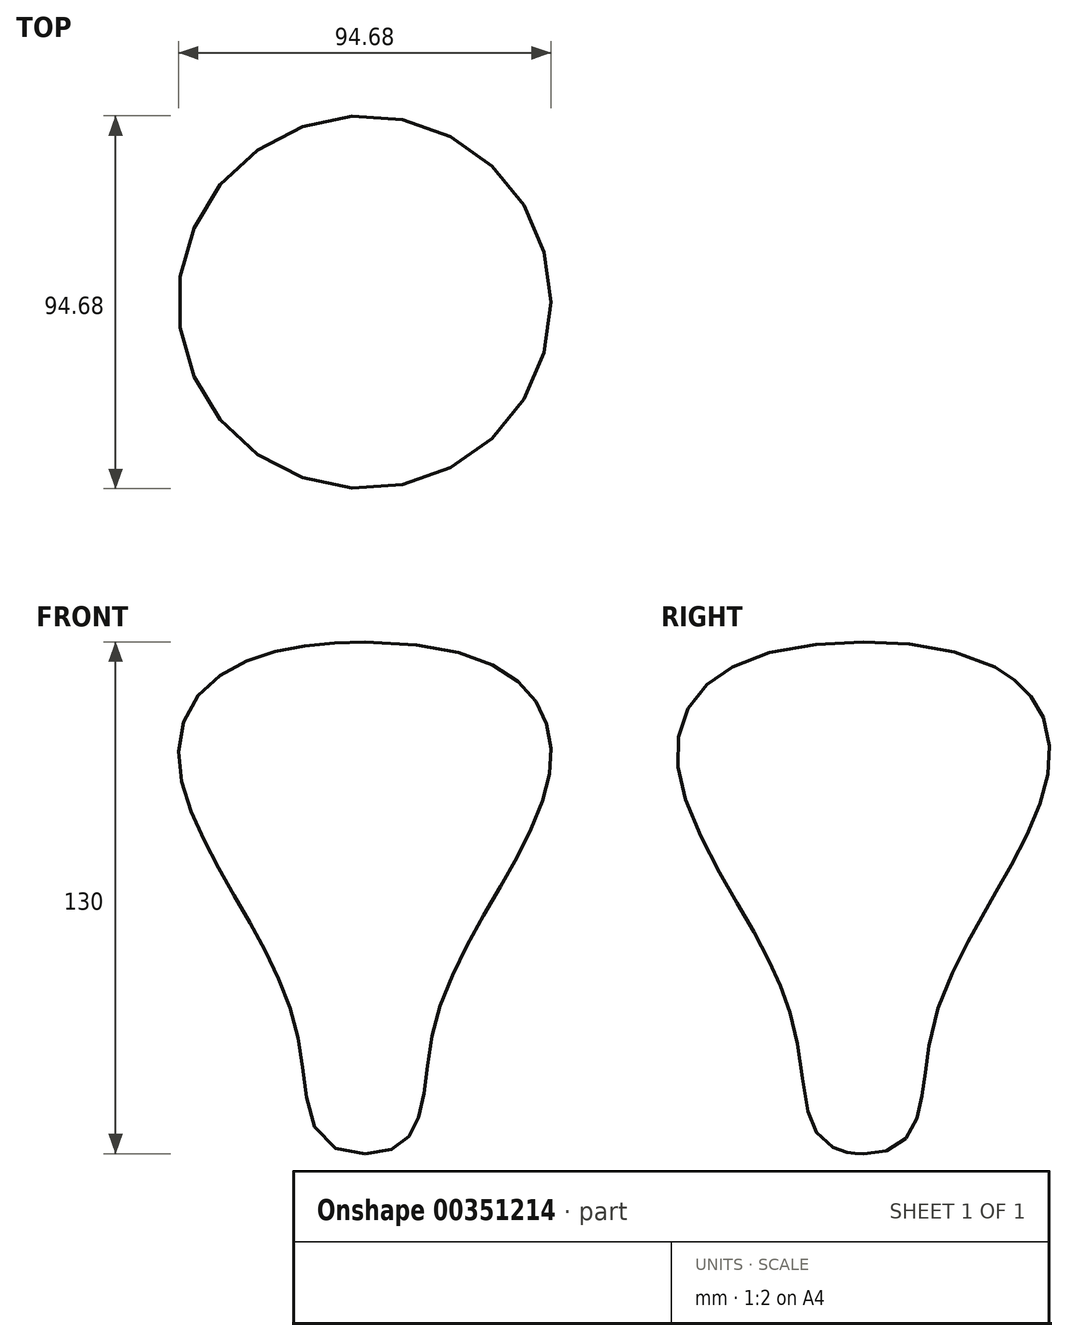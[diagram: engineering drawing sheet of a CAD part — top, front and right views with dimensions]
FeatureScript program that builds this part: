
annotation { "Feature Type Name" : "Feature", "Feature Type Description" : "" }
export const myFeature = defineFeature(function(context is Context, id is Id, definition is map)
    precondition{}
    {
        {
            var Q0;
            Q0=qCreatedBy(makeId("Front.planeOp"),FACE);
            var sketch = newSketch(context, id + "F0", { "sketchPlane" : qUnion([Q0])});
            skFitSpline(sketch, "E0", {"points": [v(0, 92.84) * mm, v(47, 60) * mm, v(17.63, -4.78) * mm, v(0, -37.16) * mm], "startDerivative": vector(329.45, 0) * mm, "endDerivative": vector(-192.32, 0) * mm});
            skLineSegment(sketch, "E1", {"start": v(0, 92.84) * mm, "end": v(0, -37.16) * mm});
            skSolve(sketch);
        }
        {
            var Q0;
            Q0 = qSketchRegion(id + "F0", true);
            var Q1;
            Q1=sQuery(id+"F0.wireOp",EDGE,"E1");
            revolve(context, id + "F1", {"entities" : qUnion([Q0]), "axis" : qUnion([Q1]), "revolveType" : RevolveType.FULL});
        }
    });
